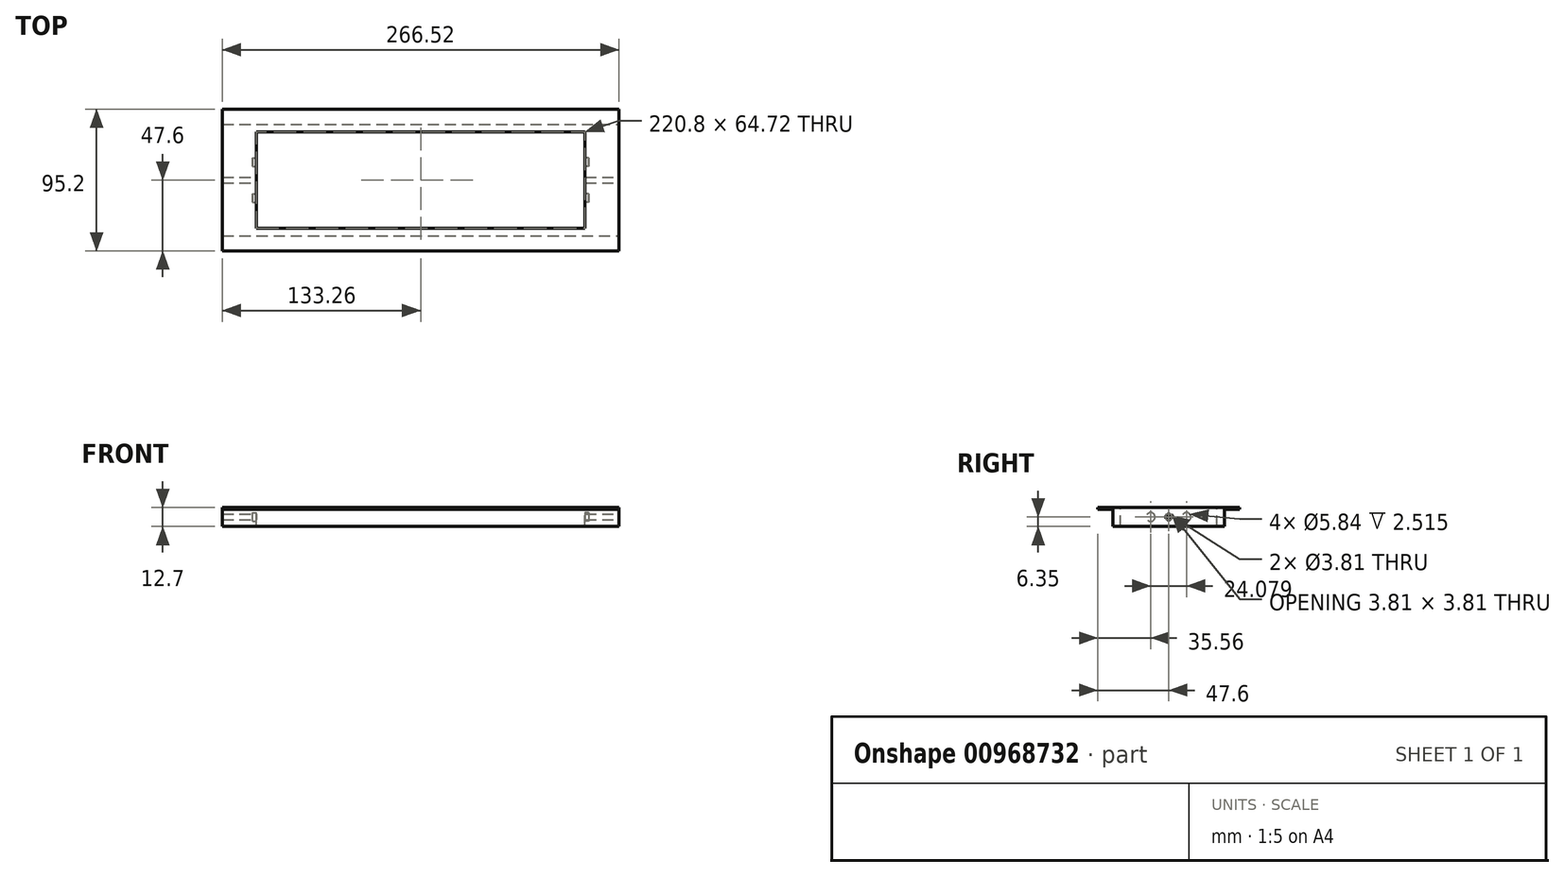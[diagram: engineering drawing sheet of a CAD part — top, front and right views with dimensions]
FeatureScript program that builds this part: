
annotation { "Feature Type Name" : "Feature", "Feature Type Description" : "" }
export const myFeature = defineFeature(function(context is Context, id is Id, definition is map)
    precondition{}
    {
        {
            var Q0;
            Q0=qCreatedBy(makeId("Top.planeOp"),FACE);
            var sketch = newSketch(context, id + "F0", { "sketchPlane" : qUnion([Q0])});
            skLineSegment(sketch, "E0.bottom", {"start": v(-133.26, 47.6) * mm, "end": v(133.26, 47.6) * mm});
            skLineSegment(sketch, "E0.top", {"start": v(-133.26, -47.6) * mm, "end": v(133.26, -47.6) * mm});
            skLineSegment(sketch, "E0.left", {"start": v(-133.26, 47.6) * mm, "end": v(-133.26, -47.6) * mm});
            skLineSegment(sketch, "E0.right", {"start": v(133.26, 47.6) * mm, "end": v(133.26, -47.6) * mm});
            skPoint(sketch, "E0.middle", {"position": v(0, 0) * mm});
            skSolve(sketch);
        }
        {
            var Q0;
            Q0=makeQuery(id+"F0.imprint","IMPRINT",FACE,{"disambiguationData":[TD([[makeQuery(id+"F0.imprint","IMPRINT",EDGE,{"derivedFrom":sQuery(id+"F0.wireOp",EDGE,"E0.bottom")}),-1.0]])]});
            extrude(context, id + "F1", {"entities" : qUnion([Q0]), "depth" : 12.7 * mm, "offsetDistance" : 25.4 * mm});
        }
        {
            var Q0;
            Q0=makeQuery(id+"F1.opExtrude","CAP_FACE",FACE,{"disambiguationData":[OSD([sQuery(id+"F0.wireOp",EDGE,"E0.bottom"),sQuery(id+"F0.wireOp",EDGE,"E0.top"),sQuery(id+"F0.wireOp",EDGE,"E0.left"),sQuery(id+"F0.wireOp",EDGE,"E0.right")])],"isStart":false});
            var sketch = newSketch(context, id + "F2", { "sketchPlane" : qUnion([Q0])});
            skLineSegment(sketch, "E1.bottom", {"start": v(-107.86, 22.2) * mm, "end": v(107.86, 22.2) * mm});
            skLineSegment(sketch, "E1.top", {"start": v(-107.86, -22.2) * mm, "end": v(107.86, -22.2) * mm});
            skLineSegment(sketch, "E1.left", {"start": v(-107.86, 22.2) * mm, "end": v(-107.86, -22.2) * mm});
            skLineSegment(sketch, "E1.right", {"start": v(107.86, 22.2) * mm, "end": v(107.86, -22.2) * mm});
            skPoint(sketch, "E1.middle", {"position": v(0, 0) * mm});
            skLineSegment(sketch, "E2.bottom", {"start": v(-110.4, 32.36) * mm, "end": v(110.4, 32.36) * mm});
            skLineSegment(sketch, "E2.top", {"start": v(-110.4, -32.36) * mm, "end": v(110.4, -32.36) * mm});
            skLineSegment(sketch, "E2.left", {"start": v(-110.4, 32.36) * mm, "end": v(-110.4, -32.36) * mm});
            skLineSegment(sketch, "E2.right", {"start": v(110.4, 32.36) * mm, "end": v(110.4, -32.36) * mm});
            skSolve(sketch);
        }
        {
            var Q0;
            Q0=makeQuery(id+"F2.imprint","IMPRINT",FACE,{"disambiguationData":[TD([[makeQuery(id+"F2.imprint","IMPRINT",EDGE,{"derivedFrom":sQuery(id+"F2.wireOp",EDGE,"E1.bottom")}),1.0]])]});
            var Q1;
            Q1=makeQuery(id+"F2.imprint","IMPRINT",FACE,{"disambiguationData":[TD([[makeQuery(id+"F2.imprint","IMPRINT",EDGE,{"derivedFrom":sQuery(id+"F2.wireOp",EDGE,"E1.bottom")}),-1.0]])]});
            extrude(context, id + "F3", {"entities" : qUnion([Q0, Q1]), "operationType" : NewBodyOperationType.REMOVE, "oppositeDirection" : true, "depth" : 25.4 * mm, "offsetDistance" : 25.4 * mm});
        }
        {
            var Q0;
            Q0=makeQuery(id+"F1.opExtrude","SWEPT_FACE",FACE,{"disambiguationData":[OSD([sQuery(id+"F0.wireOp",EDGE,"E0.right")])]});
            var sketch = newSketch(context, id + "F4", { "sketchPlane" : qUnion([Q0])});
            skCircle(sketch, "E3", {"center": v(0, 6.35) * mm, "radius": 1.9 * mm});
            skSolve(sketch);
        }
        {
            var Q0;
            Q0=makeQuery(id+"F4.imprint","IMPRINT",FACE,{"disambiguationData":[TD([[makeQuery(id+"F4.imprint","IMPRINT",EDGE,{"derivedFrom":sQuery(id+"F4.wireOp",EDGE,"E3")}),1.0]])]});
            extrude(context, id + "F5", {"entities" : qUnion([Q0]), "operationType" : NewBodyOperationType.REMOVE, "oppositeDirection" : true, "depth" : 508 * mm, "offsetDistance" : 25.4 * mm});
        }
        {
            var Q0;
            Q0=makeQuery(id+"F3.boolean.opBoolean","COPY",FACE,{"derivedFrom":makeQuery(id+"F3.opExtrude","SWEPT_FACE",FACE,{"disambiguationData":[OSD([sQuery(id+"F2.wireOp",EDGE,"E2.left")])]})});
            var sketch = newSketch(context, id + "F6", { "sketchPlane" : qUnion([Q0])});
            skCircle(sketch, "E4", {"center": v(-12.04, 6.35) * mm, "radius": 2.92 * mm});
            skPoint(sketch, "E4.centerSnap0", {"position": v(-32.36, 6.35) * mm});
            skCircle(sketch, "E5", {"center": v(12.04, 6.35) * mm, "radius": 2.92 * mm});
            skPoint(sketch, "E5.centerSnap0", {"position": v(32.36, 6.35) * mm});
            skSolve(sketch);
        }
        {
            var Q0;
            Q0=makeQuery(id+"F6.imprint","IMPRINT",FACE,{"disambiguationData":[TD([[makeQuery(id+"F6.imprint","IMPRINT",EDGE,{"derivedFrom":sQuery(id+"F6.wireOp",EDGE,"E4")}),1.0]])]});
            var Q1;
            Q1=makeQuery(id+"F6.imprint","IMPRINT",FACE,{"disambiguationData":[TD([[makeQuery(id+"F6.imprint","IMPRINT",EDGE,{"derivedFrom":sQuery(id+"F6.wireOp",EDGE,"E5")}),1.0]])]});
            extrude(context, id + "F7", {"entities" : qUnion([Q0, Q1]), "operationType" : NewBodyOperationType.REMOVE, "oppositeDirection" : true, "depth" : 2.5 * mm, "offsetDistance" : 25.4 * mm});
        }
        {
            var Q0;
            Q0=makeQuery(id+"F3.boolean.opBoolean","COPY",FACE,{"derivedFrom":makeQuery(id+"F3.opExtrude","SWEPT_FACE",FACE,{"disambiguationData":[OSD([sQuery(id+"F2.wireOp",EDGE,"E2.right")])]})});
            var sketch = newSketch(context, id + "F8", { "sketchPlane" : qUnion([Q0])});
            skCircle(sketch, "E6", {"center": v(-12.04, 6.35) * mm, "radius": 2.92 * mm});
            skPoint(sketch, "E6.centerSnap0", {"position": v(-32.36, 6.35) * mm});
            skCircle(sketch, "E7", {"center": v(12.04, 6.35) * mm, "radius": 2.92 * mm});
            skPoint(sketch, "E7.centerSnap0", {"position": v(32.36, 6.35) * mm});
            skSolve(sketch);
        }
        {
            var Q0;
            Q0=makeQuery(id+"F8.imprint","IMPRINT",FACE,{"disambiguationData":[TD([[makeQuery(id+"F8.imprint","IMPRINT",EDGE,{"derivedFrom":sQuery(id+"F8.wireOp",EDGE,"E6")}),1.0]])]});
            var Q1;
            Q1=makeQuery(id+"F8.imprint","IMPRINT",FACE,{"disambiguationData":[TD([[makeQuery(id+"F8.imprint","IMPRINT",EDGE,{"derivedFrom":sQuery(id+"F8.wireOp",EDGE,"E7")}),1.0]])]});
            extrude(context, id + "F9", {"entities" : qUnion([Q0, Q1]), "operationType" : NewBodyOperationType.REMOVE, "oppositeDirection" : true, "depth" : 2.5 * mm, "offsetDistance" : 25.4 * mm});
        }
        {
            var Q0;
            Q0=makeQuery(id+"F1.opExtrude","SWEPT_FACE",FACE,{"disambiguationData":[OSD([sQuery(id+"F0.wireOp",EDGE,"E0.right")])]});
            var sketch = newSketch(context, id + "F10", { "sketchPlane" : qUnion([Q0])});
            skLineSegment(sketch, "E8.bottom", {"start": v(-47.6, 0) * mm, "end": v(-37.44, 0) * mm});
            skLineSegment(sketch, "E8.top", {"start": v(-47.6, 11.43) * mm, "end": v(-37.44, 11.43) * mm});
            skLineSegment(sketch, "E8.left", {"start": v(-47.6, 0) * mm, "end": v(-47.6, 11.43) * mm});
            skLineSegment(sketch, "E8.right", {"start": v(-37.44, 0) * mm, "end": v(-37.44, 11.43) * mm});
            skLineSegment(sketch, "E9.bottom", {"start": v(47.6, 0) * mm, "end": v(37.44, 0) * mm});
            skLineSegment(sketch, "E9.top", {"start": v(47.6, 11.43) * mm, "end": v(37.44, 11.43) * mm});
            skLineSegment(sketch, "E9.left", {"start": v(47.6, 0) * mm, "end": v(47.6, 11.43) * mm});
            skLineSegment(sketch, "E9.right", {"start": v(37.44, 0) * mm, "end": v(37.44, 11.43) * mm});
            skSolve(sketch);
        }
        {
            var Q0;
            Q0=makeQuery(id+"F10.imprint","IMPRINT",FACE,{"disambiguationData":[TD([[makeQuery(id+"F10.imprint","IMPRINT",EDGE,{"derivedFrom":sQuery(id+"F10.wireOp",EDGE,"E8.bottom")}),-1.0]])]});
            var Q1;
            Q1=makeQuery(id+"F10.imprint","IMPRINT",FACE,{"disambiguationData":[TD([[makeQuery(id+"F10.imprint","IMPRINT",EDGE,{"derivedFrom":sQuery(id+"F10.wireOp",EDGE,"E9.bottom")}),-1.0]])]});
            extrude(context, id + "F11", {"entities" : qUnion([Q0, Q1]), "operationType" : NewBodyOperationType.REMOVE, "oppositeDirection" : true, "depth" : 508 * mm, "offsetDistance" : 25.4 * mm});
        }
    });
